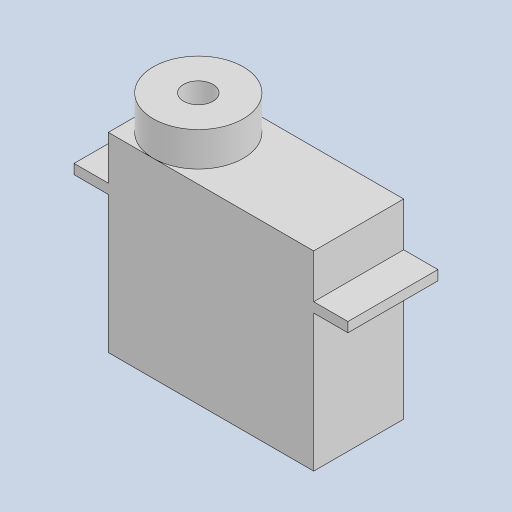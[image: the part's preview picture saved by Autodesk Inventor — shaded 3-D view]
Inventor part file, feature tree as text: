
AUTODESK INVENTOR PART (.ipt)
format: ipt  version: 2023 (Build 270158000, 158)  size: 126,976 bytes
history: native  units: in
note: dims shown in document units (in); Inventor stores cm internally (conversion verified against a paired STEP export)
features: sketch x5, extrude x4, other x1, hole x1
ambient origin geometry x8: Origin, YZ Plane, XZ Plane, XY Plane, X Axis, Y Axis, Z Axis, Center Point
bodies: Body1 (feature_tree)
feature tree (11):
  other  "ソリッド1"
  sketch  "スケッチ1"
  extrude  "押し出し1"  Depth=0.8268in
  extrude  "押し出し2"  Depth=0.3622in
  extrude  "押し出し3"  Depth=0.5512in TaperAngle=0.0deg
  extrude  "押し出し4"  Depth=0.1378in
  hole  "穴1"  [1 undecoded]
  sketch  "スケッチ2"
  sketch  "スケッチ3"
  sketch  "スケッチ4"
  sketch  "スケッチ5"
note: 1 required parameter value undecoded (feature->parameter linkage not recoverable at this tier; creation-order binding heuristic only, values carry confidence <= 0.55)
